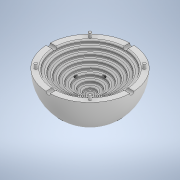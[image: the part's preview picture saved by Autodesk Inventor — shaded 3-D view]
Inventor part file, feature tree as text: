
AUTODESK INVENTOR PART (.ipt)
format: ipt  version: 2022 (Build 260153000, 153)  size: 522,240 bytes
history: native  units: mm
features: extrude x16, sketch x16, other x9, fillet x5
ambient origin geometry x8: Origin, YZ Plane, XZ Plane, XY Plane, X Axis, Y Axis, Z Axis, Center Point
bodies: Body1 (feature_tree)
feature tree (46):
  other  "實體1"
  extrude  "擠出1"  Depth=60.0mm
  fillet  "圓角1"  Radius=30.0mm
  extrude  "擠出2"  Depth=30.0mm
  extrude  "擠出3"  Depth=50.0mm
  extrude  "擠出4"  Depth=2.0mm TaperAngle=0.0deg
  extrude  "擠出5"  Depth=44.0mm
  extrude  "擠出6"  Depth=2.0mm TaperAngle=0.0deg
  extrude  "擠出7"  Depth=38.0mm
  extrude  "擠出8"  Depth=2.0mm TaperAngle=0.0deg
  extrude  "擠出9"  Depth=32.0mm
  extrude  "擠出11"  Depth=2.0mm TaperAngle=0.0deg
  extrude  "擠出12"  Depth=26.0mm
  extrude  "擠出13"  Depth=2.0mm TaperAngle=0.0deg
  extrude  "擠出16"  Depth=20.0mm
  fillet  "圓角2"  Radius=2.0mm
  extrude  "擠出17"  Depth=14.0mm
  fillet  "圓角3"  Radius=2.0mm
  extrude  "擠出18"  Depth=8.0mm
  fillet  "圓角4"  Radius=2.0mm
  extrude  "擠出19"  Depth=3.0mm
  fillet  "圓角5"  Radius=20.0mm
  other  "面圓角1"
  other  "面圓角2"
  other  "面圓角3"
  other  "面圓角4"
  other  "面圓角5"
  other  "面圓角6"
  other  "面圓角7"
  other  "面圓角8"
  sketch  "草圖3"
  sketch  "草圖4"
  sketch  "草圖5"
  sketch  "草圖6"
  sketch  "草圖7"
  sketch  "草圖8"
  sketch  "草圖9"
  sketch  "草圖10"
  sketch  "草圖11"
  sketch  "草圖14"
  sketch  "草圖15"
  sketch  "草圖16"
  sketch  "草圖25"
  sketch  "草圖26"
  sketch  "草圖27"
  sketch  "草圖29"
